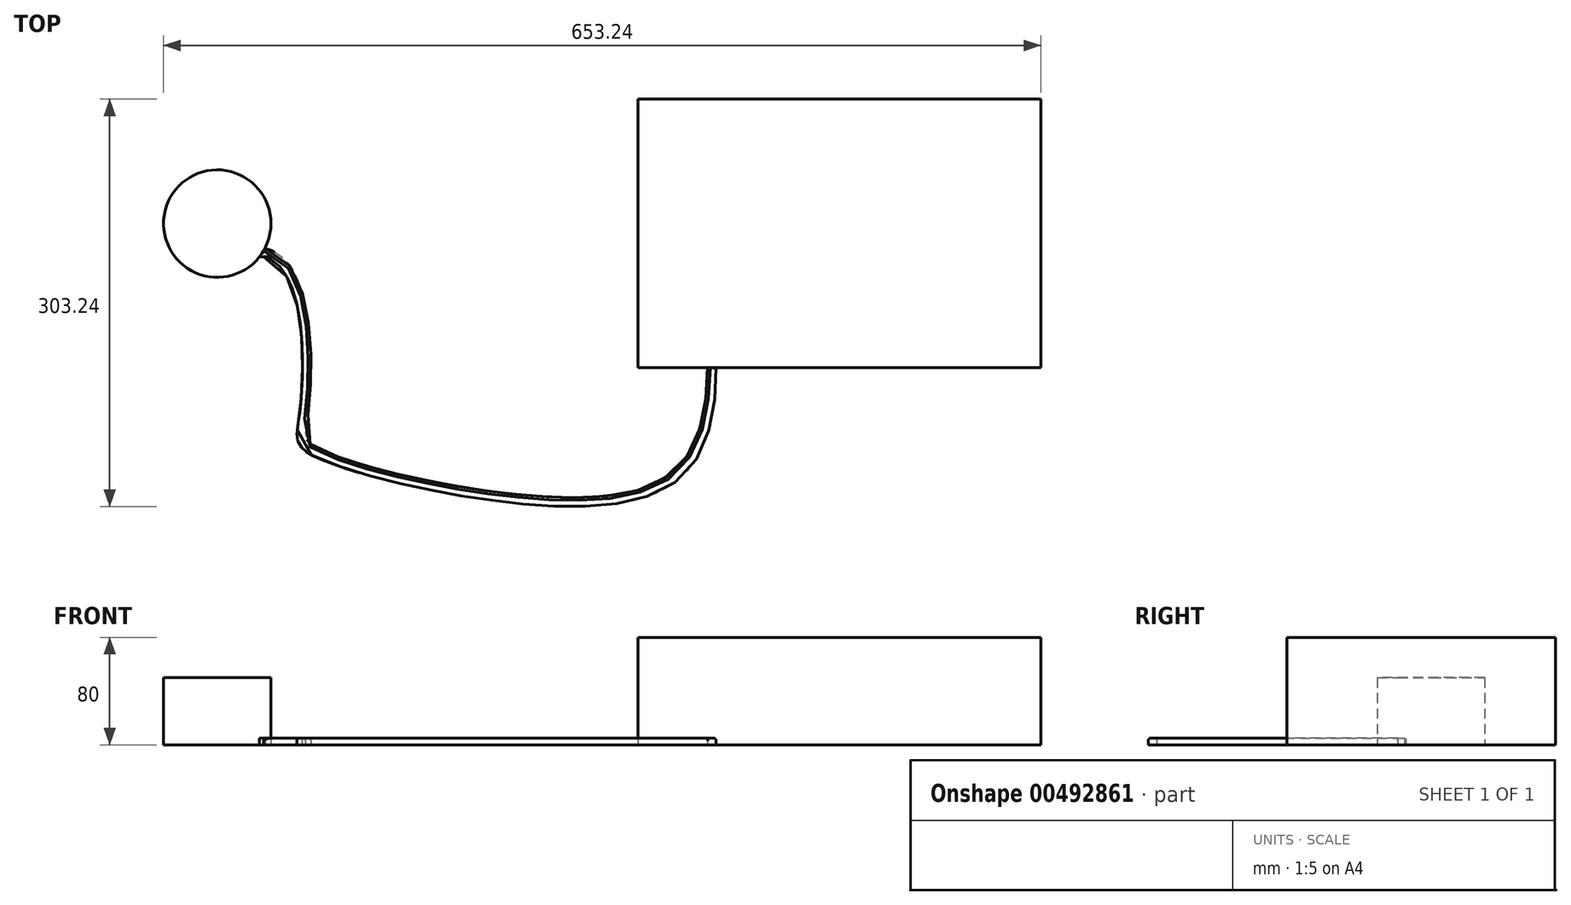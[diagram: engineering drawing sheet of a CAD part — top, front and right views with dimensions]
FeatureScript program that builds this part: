
annotation { "Feature Type Name" : "Feature", "Feature Type Description" : "" }
export const myFeature = defineFeature(function(context is Context, id is Id, definition is map)
    precondition{}
    {
        {
            var Q0;
            Q0=qCreatedBy(makeId("Top.planeOp"),FACE);
            var sketch = newSketch(context, id + "F0", { "sketchPlane" : qUnion([Q0])});
            skLineSegment(sketch, "E0.bottom", {"start": v(0, 0) * mm, "end": v(300, 0) * mm});
            skLineSegment(sketch, "E0.top", {"start": v(0, 200) * mm, "end": v(300, 200) * mm});
            skLineSegment(sketch, "E0.left", {"start": v(0, 0) * mm, "end": v(0, 200) * mm});
            skLineSegment(sketch, "E0.right", {"start": v(300, 0) * mm, "end": v(300, 200) * mm});
            skSolve(sketch);
        }
        {
            var Q0;
            Q0 = qSketchRegion(id + "F0", true);
            extrude(context, id + "F1", {"entities" : qUnion([Q0]), "depth" : 80 * mm});
        }
        {
            var Q0;
            Q0=qCreatedBy(makeId("Top.planeOp"),FACE);
            var sketch = newSketch(context, id + "F2", { "sketchPlane" : qUnion([Q0])});
            skCircle(sketch, "E1", {"center": v(-313.24, 107.4) * mm, "radius": 40 * mm});
            skSolve(sketch);
        }
        {
            var Q0;
            Q0 = qSketchRegion(id + "F2", true);
            extrude(context, id + "F3", {"entities" : qUnion([Q0]), "depth" : 50 * mm});
        }
        {
            var Q0;
            Q0=qCreatedBy(makeId("Top.planeOp"),FACE);
            var sketch = newSketch(context, id + "F4", { "sketchPlane" : qUnion([Q0])});
            skFitSpline(sketch, "E2", {"points": [v(-277.46, 88.82) * mm, v(-245.95, -37.2) * mm, v(-241.57, -58.33) * mm, v(-13.86, -94.22) * mm, v(51.94, 0) * mm], "startDerivative": vector(431.5, -96.87) * mm, "endDerivative": vector(9.36, 670.7) * mm});
            skFitSpline(sketch, "E3.0", {"points": [v(-278.85, 82.62) * mm, v(-277.1, 82.23) * mm, v(-273.89, 81.07) * mm, v(-269.59, 78.23) * mm, v(-265.66, 74.23) * mm, v(-262.12, 69.07) * mm, v(-259.03, 62.86) * mm, v(-255.53, 53.37) * mm, v(-252.36, 39.67) * mm, v(-250.3, 21.67) * mm, v(-249.76, 6.47) * mm, v(-249.87, -5.18) * mm, v(-250.18, -13.5) * mm, v(-250.66, -21.26) * mm, v(-251.17, -27.11) * mm, v(-251.62, -31.35) * mm, v(-251.9, -33.79) * mm, v(-252.14, -35.61) * mm, v(-252.38, -37.34) * mm, v(-252.8, -40.16) * mm, v(-253.26, -43) * mm, v(-253.61, -45.64) * mm, v(-253.8, -47.58) * mm, v(-253.87, -49.53) * mm, v(-253.77, -51.56) * mm, v(-253.4, -53.68) * mm, v(-252.66, -55.82) * mm, v(-251.55, -57.84) * mm, v(-250.14, -59.63) * mm, v(-248.53, -61.18) * mm, v(-246.76, -62.55) * mm, v(-244.83, -63.8) * mm, v(-242.68, -65.03) * mm, v(-240.3, -66.25) * mm, v(-236.83, -67.88) * mm, v(-231.89, -69.95) * mm, v(-225.04, -72.5) * mm, v(-217.34, -75.1) * mm, v(-208.85, -77.72) * mm, v(-199.63, -80.35) * mm, v(-186.5, -83.83) * mm, v(-168.66, -88.07) * mm, v(-145.63, -92.77) * mm, v(-121.63, -96.86) * mm, v(-97.29, -100.11) * mm, v(-73.25, -102.32) * mm, v(-50.14, -103.24) * mm, v(-32.16, -102.74) * mm, v(-18.84, -101.45) * mm, v(-9.45, -100) * mm, v(-0.71, -98.02) * mm, v(10.1, -94.67) * mm, v(22.08, -89.06) * mm, v(34, -79.89) * mm, v(43.35, -68.32) * mm, v(50.2, -54.54) * mm, v(54.82, -38.68) * mm, v(57.5, -20.7) * mm, v(58.19, -7.22) * mm, v(58.29, -0.09) * mm]});
            skLineSegment(sketch, "E4", {"start": v(-278.85, 82.62) * mm, "end": v(-283.04, 82.62) * mm});
            skLineSegment(sketch, "E5", {"start": v(-283.04, 82.62) * mm, "end": v(-277.46, 88.82) * mm});
            skLineSegment(sketch, "E6", {"start": v(51.94, 0) * mm, "end": v(58.29, -0.09) * mm});
            skSolve(sketch);
        }
        {
            var Q0;
            Q0 = qSketchRegion(id + "F4", true);
            extrude(context, id + "F5", {"entities" : qUnion([Q0]), "operationType" : NewBodyOperationType.ADD, "depth" : 5 * mm});
        }
        {
            var Q0;
            Q0=makeQuery(id+"F5.opExtrude","CAP_EDGE",EDGE,{"disambiguationData":[OSD([sQuery(id+"F4.wireOp",EDGE,"E3.0")])],"isStart":false});
            var Q1;
            Q1=makeQuery(id+"F5.opExtrude","CAP_EDGE",EDGE,{"disambiguationData":[OSD([sQuery(id+"F4.wireOp",EDGE,"E2")])],"isStart":false});
            fillet(context, id + "F6", {"entities" : qUnion([Q0, Q1]), "radius" : 2 * mm, "tangentPropagation" : true, "allowEdgeOverflow" : false});
        }
    });
